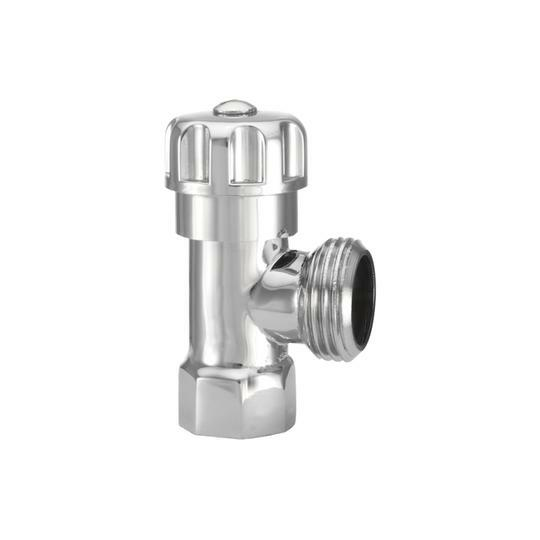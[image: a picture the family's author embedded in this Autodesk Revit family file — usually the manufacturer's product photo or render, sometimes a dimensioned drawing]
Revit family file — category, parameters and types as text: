
# Revit family: 01-9915-11 LLAVE LAVADORA METAL CROMO
name_source: partatom
category: Aparatos sanitarios
revit_build: Autodesk Revit 2018 (Build: 20170223_1515(x64)
units: mm (PartAtom-declared; Revit-internal decimal feet)

## family parameters
Anfitrión = Cara
Compartido = No
Corte con vacíos al cargar = No
Cota de conector redondo = Diámetro de uso
Número OmniClass = 23.31.11.00
Punto de cálculo de habitación = No
Tipo de pieza = Normal

## types (1)
- 01-9915-11
    Alto = 70 mm  [stored 0.229659 ft]
    Conexión AC = Sí
    Conexión AF = Sí
    Conexión de residuos = No
    Conexión de ventilación = No
    Descripción = Llave
    Dim Manija = 30.4 mm
    Elevación por defecto = 0 mm  [stored 0 ft]
    Fabricante = Gricol
    Imagen de tipo = LLAVE LAVADORA METAL CROMO.jpg
    Link Ficha Tecnica = http://infotecnica.gricol.com
    Metal  Laton cromado = Metal Laton Cromado
    Modelo = 01-9915-11
    Plastico ABS Cromado = Plastico - ABS Cromado
    Product Name = LLAVE LAVADORA METAL CROMO
    Rosca NH 3/4" = 3/4"
    Rosca NPT 1/2" = 1/2"
    URL = https://www.gricol.com

note: [stored X ft] marks values corroborated as IEEE doubles in the binary element streams (Revit-internal decimal feet)

## geometry (parser evidence)
native form markers: Blend x2, Sweep x6
no freeform markers — native parametric forms only
